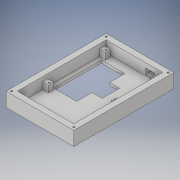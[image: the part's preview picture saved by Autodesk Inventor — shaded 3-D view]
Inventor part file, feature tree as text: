
AUTODESK INVENTOR PART (.ipt)
format: ipt  version: 2019 (Build 230136000, 136)  size: 232,960 bytes
history: native  units: in
note: dims shown in document units (in); Inventor stores cm internally (conversion verified against a paired STEP export)
features: thread x8, sketch x7, extrude x5, hole x2
ambient origin geometry x8: Origin, YZ Plane, XZ Plane, XY Plane, X Axis, Y Axis, Z Axis, Center Point
bodies: Solid1 (feature_tree)
feature tree (22):
  extrude  "Extrusion1"  Depth=4.7441in
  extrude  "Extrusion2"  Depth=6.2205in
  extrude  "Extrusion3"  Depth=0.3937in
  extrude  "Extrusion4"  Depth=0.7874in TaperAngle=0.0deg
  hole  "Hole1"  [1 undecoded]
  thread  "Thread1"  [1 undecoded]
  thread  "Thread2"  [1 undecoded]
  thread  "Thread3"  [1 undecoded]
  thread  "Thread4"  [1 undecoded]
  hole  "Hole2"  [1 undecoded]
  thread  "Thread5"  [1 undecoded]
  thread  "Thread6"  [1 undecoded]
  thread  "Thread7"  [1 undecoded]
  thread  "Thread8"  [1 undecoded]
  extrude  "Extrusion5"  Depth=0.4134in
  sketch  "Sketch1"  dims[d1=7.0079in d2=4.7441in]
  sketch  "Sketch2"  dims[d3=0.9843in d4=0.0in d5=6.2205in]
  sketch  "Sketch3"  dims[d6=3.9567in d7=0.3937in]
  sketch  "Sketch4"  dims[d8=0.3937in d9=0.7874in d10=0.0in]
  sketch  "Sketch6"  dims[d11=2.2441in d12=0.5906in d13=0.2559in d14=0.0in d15=1.6535in d16=1.3386in]
  sketch  "Sketch7"  dims[d17=1.6732in d18=3.3268in d19=1.6339in d20=1.752in d21=0.5512in d22=0.7874in d23=0.0in]
  sketch  "Sketch8"  dims[d24=0.0in d25=0.4134in d26=0.3543in d27=0.1181in d28=1.6929in d29=2.372in d30=1.1811in d31=0.4724in d32=0.0in d33=0.1181in d34=0.2953in d35=0.1772in d36=1.6929in d37=1.6929in d38=4.3307in d39=0.1772in d40=0.2953in d41=2.372in d42=1.1811in d43=2.7165in d44=0.2953in d45=0.2953in d46=0.1772in d47=0.1181in d48=0.2953in d49=0.1476in d50=0.0984in d51=90.0deg d52=0.3937in d53=0.8108in d54=0.3937in d55=0.0in d56=0.3937in d57=0.0in d58=0.3937in d59=0.0in d60=0.3937in d61=0.0in d62=0.1181in d63=0.1969in d64=0.1969in d65=3.5039in d66=2.372in d67=0.1181in d68=0.2953in d69=0.1476in d70=0.0984in d71=90.0deg d72=0.7874in d73=0.8108in d74=0.3937in d75=0.0in d76=0.3937in d77=0.0in d78=0.3937in d79=0.0in d80=0.3937in d81=0.0in d82=0.5512in d83=0.6299in d84=0.315in d85=0.0787in d86=0.4724in d87=0.0in]
note: 10 required parameter values undecoded (feature->parameter linkage not recoverable at this tier; creation-order binding heuristic only, values carry confidence <= 0.55)
